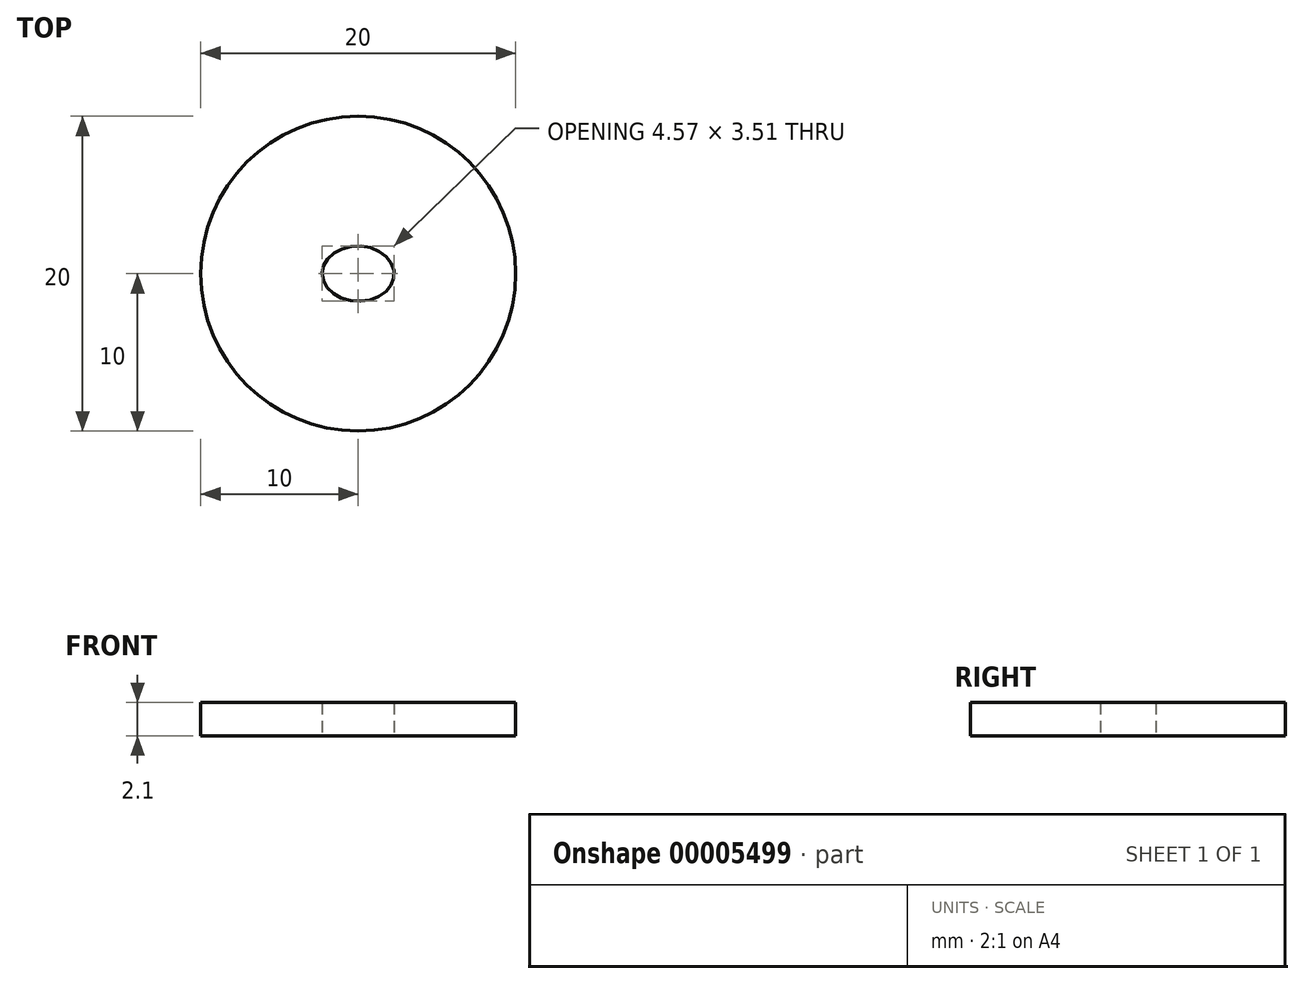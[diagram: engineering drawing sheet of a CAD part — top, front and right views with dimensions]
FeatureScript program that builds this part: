
annotation { "Feature Type Name" : "Feature", "Feature Type Description" : "" }
export const myFeature = defineFeature(function(context is Context, id is Id, definition is map)
    precondition{}
    {
        {
            var Q0;
            Q0=qCreatedBy(makeId("Top.planeOp"),FACE);
            var sketch = newSketch(context, id + "F0", { "sketchPlane" : qUnion([Q0])});
            skCircle(sketch, "E0", {"center": v(0, 0) * mm, "radius": 10 * mm});
            skLineSegment(sketch, "E1.bottom", {"start": v(-2.25, 1.75) * mm, "end": v(2.25, 1.75) * mm, "construction": true});
            skLineSegment(sketch, "E1.top", {"start": v(-2.25, -1.75) * mm, "end": v(2.25, -1.75) * mm, "construction": true});
            skLineSegment(sketch, "E1.left", {"start": v(-2.25, 1.75) * mm, "end": v(-2.25, -1.75) * mm, "construction": true});
            skLineSegment(sketch, "E1.right", {"start": v(2.25, 1.75) * mm, "end": v(2.25, -1.75) * mm, "construction": true});
            skEllipse(sketch, "E2", {"center": v(0, 0) * mm, "majorRadius": 2.28 * mm, "minorRadius": 1.76 * mm, "majorAxis": v(-1, 0.01)});
            skSolve(sketch);
        }
        {
            var Q0;
            Q0 = qSketchRegion(id + "F0", true);
            extrude(context, id + "F1", {"entities" : qUnion([Q0]), "depth" : 2.1 * mm});
        }
    });
